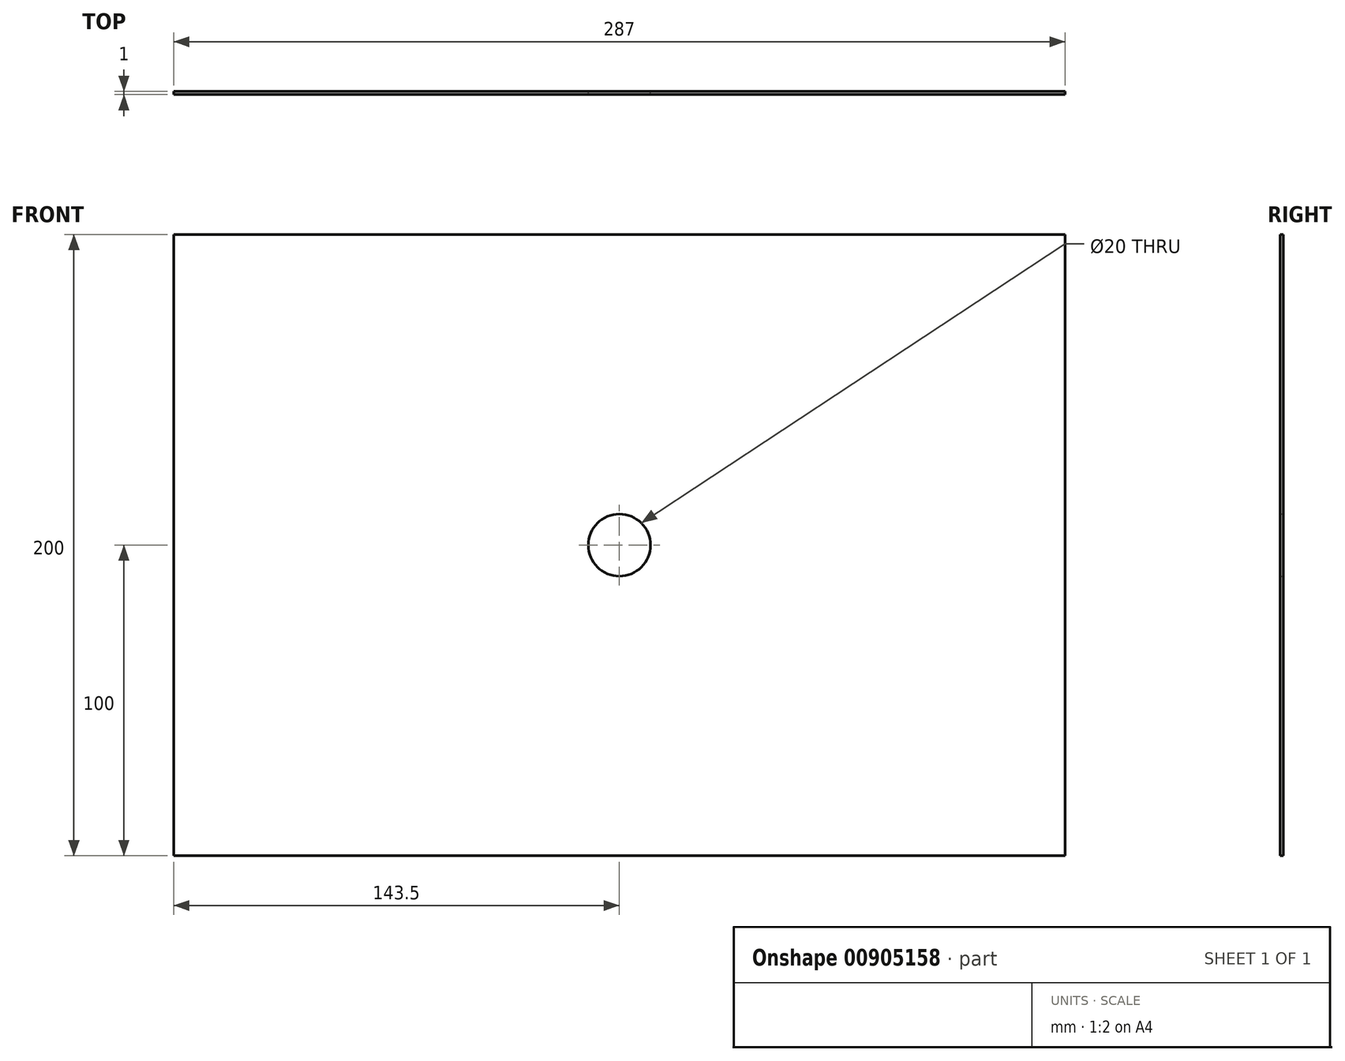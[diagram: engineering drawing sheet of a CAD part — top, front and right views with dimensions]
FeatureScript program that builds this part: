
annotation { "Feature Type Name" : "Feature", "Feature Type Description" : "" }
export const myFeature = defineFeature(function(context is Context, id is Id, definition is map)
    precondition{}
    {
        {
            var Q0;
            Q0=qCreatedBy(makeId("Front.planeOp"),FACE);
            var sketch = newSketch(context, id + "F0", { "sketchPlane" : qUnion([Q0])});
            skLineSegment(sketch, "E0.bottom", {"start": v(143.5, -100) * mm, "end": v(-143.5, -100) * mm});
            skLineSegment(sketch, "E0.top", {"start": v(143.5, 100) * mm, "end": v(-143.5, 100) * mm});
            skLineSegment(sketch, "E0.left", {"start": v(143.5, -100) * mm, "end": v(143.5, 100) * mm});
            skLineSegment(sketch, "E0.right", {"start": v(-143.5, -100) * mm, "end": v(-143.5, 100) * mm});
            skPoint(sketch, "E0.middle", {"position": v(0, 0) * mm});
            skCircle(sketch, "E1", {"center": v(0, 0) * mm, "radius": 10 * mm});
            skSolve(sketch);
        }
        {
            var Q0;
            Q0=makeQuery(id+"F0.imprint","IMPRINT",FACE,{"disambiguationData":[TD([[makeQuery(id+"F0.imprint","IMPRINT",EDGE,{"derivedFrom":sQuery(id+"F0.wireOp",EDGE,"E0.bottom")}),-1.0]])]});
            extrude(context, id + "F1", {"entities" : qUnion([Q0]), "depth" : 1 * mm, "offsetDistance" : 25 * mm});
        }
    });
